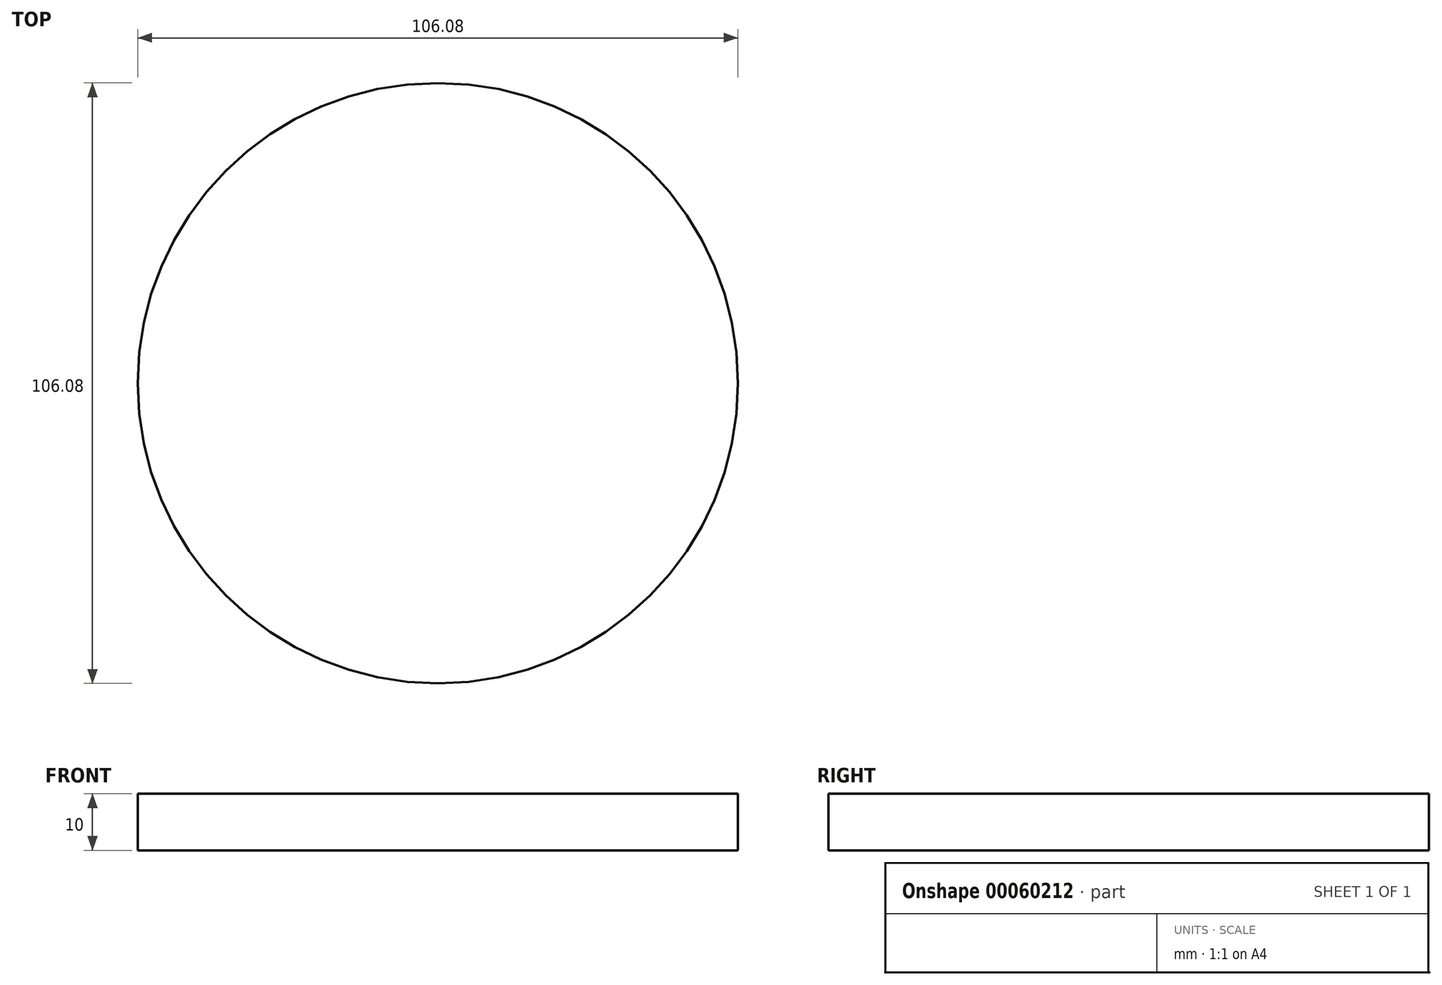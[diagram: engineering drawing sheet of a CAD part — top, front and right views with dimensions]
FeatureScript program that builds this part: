
annotation { "Feature Type Name" : "Feature", "Feature Type Description" : "" }
export const myFeature = defineFeature(function(context is Context, id is Id, definition is map)
    precondition{}
    {
        {
            var Q0;
            Q0=qCreatedBy(makeId("Top.planeOp"),FACE);
            var sketch = newSketch(context, id + "F0", { "sketchPlane" : qUnion([Q0])});
            skCircle(sketch, "E0", {"center": v(0, 0) * mm, "radius": 53.04 * mm});
            skSolve(sketch);
        }
        {
            var Q0;
            Q0=makeQuery(id+"F0.imprint","IMPRINT",FACE,{"disambiguationData":[TD([[makeQuery(id+"F0.imprint","IMPRINT",EDGE,{"derivedFrom":sQuery(id+"F0.wireOp",EDGE,"E0")}),1.0]])]});
            extrude(context, id + "F1", {"entities" : qUnion([Q0]), "depth" : 10 * mm});
        }
    });
